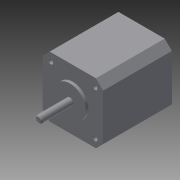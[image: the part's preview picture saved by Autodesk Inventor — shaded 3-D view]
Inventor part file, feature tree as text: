
AUTODESK INVENTOR PART (.ipt)
format: ipt  version: 2015 SP1 (Build 190203100, 203)  size: 123,392 bytes
history: native  units: in
note: dims shown in document units (in); Inventor stores cm internally (conversion verified against a paired STEP export)
features: sketch x3, extrude x1, revolve x1, hole x1
ambient origin geometry x8: Origin, YZ Plane, XZ Plane, XY Plane, X Axis, Y Axis, Z Axis, Center Point
bodies: Solid1 (feature_tree)
feature tree (6):
  extrude  "Extrusion1"  Depth=1.6654in
  revolve  "Revolution1"  [1 undecoded]
  hole  "Hole1"  [1 undecoded]
  sketch  "Sketch1"  dims[d0=1.6654in d1=1.6654in]
  sketch  "Sketch2"  dims[d2=0.1969in d3=0.1969in]
  sketch  "Sketch3"  dims[d4=0.1969in d5=0.1969in d6=0.1969in d7=0.1969in d8=0.1969in d9=0.1969in d10=1.8898in d11=0.0in d12=0.9449in d13=0.0787in d14=0.0984in d15=0.4331in d16=90.0deg d17=0.0315in d18=0.0315in d19=1.2205in d20=1.2205in d21=0.1339in d22=0.2362in d23=0.1575in d24=0.0787in d25=90.0deg d26=0.1772in d27=0.8108in]
note: 2 required parameter values undecoded (feature->parameter linkage not recoverable at this tier; creation-order binding heuristic only, values carry confidence <= 0.55)